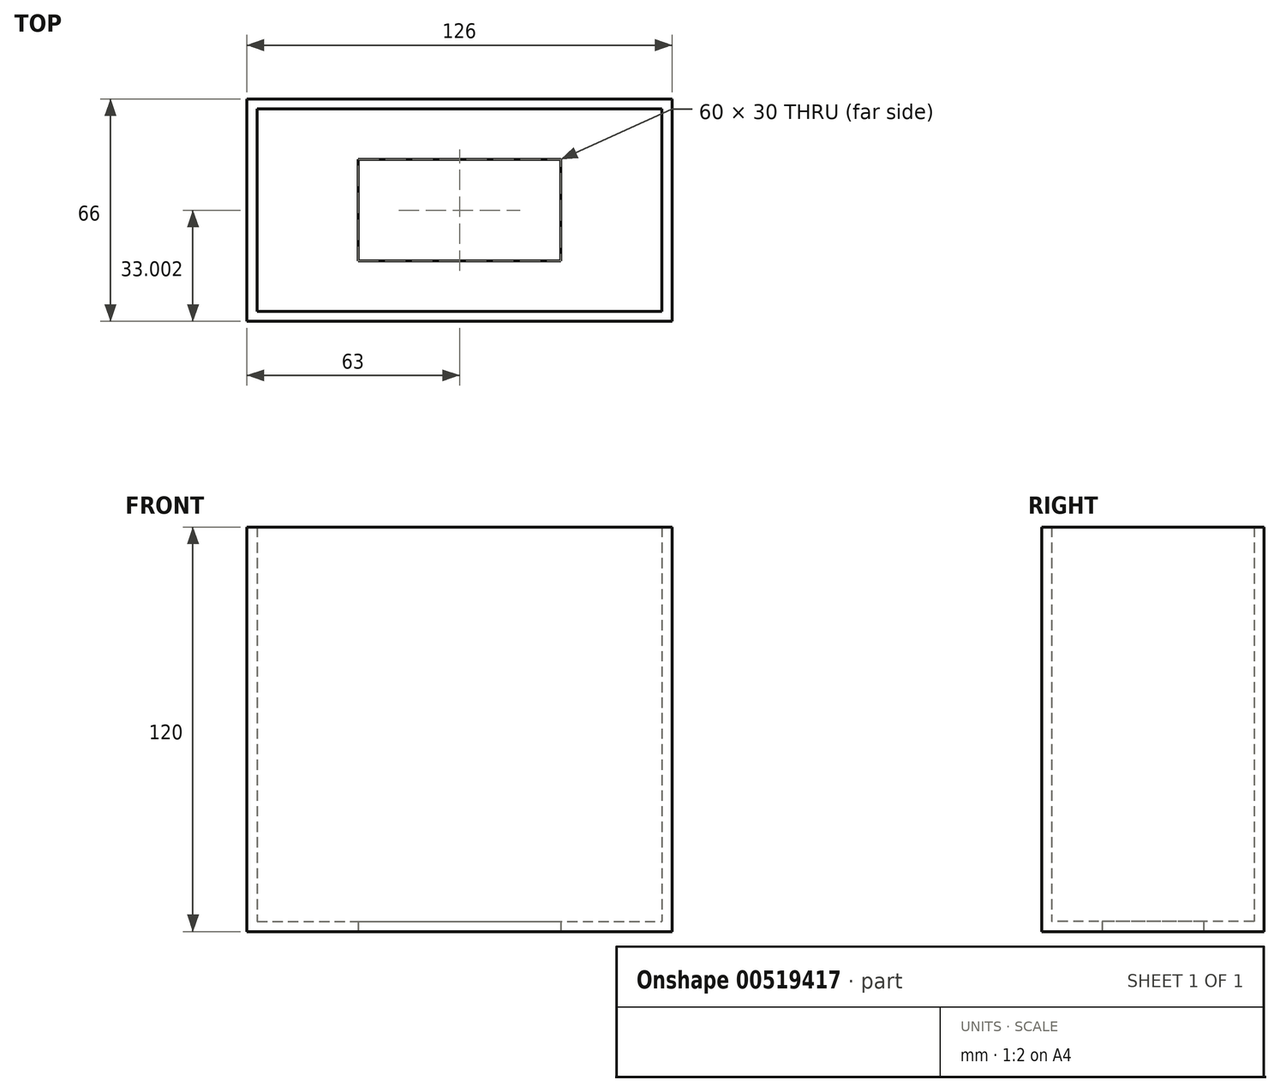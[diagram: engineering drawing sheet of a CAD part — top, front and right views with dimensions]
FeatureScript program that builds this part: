
annotation { "Feature Type Name" : "Feature", "Feature Type Description" : "" }
export const myFeature = defineFeature(function(context is Context, id is Id, definition is map)
    precondition{}
    {
        {
            var Q0;
            Q0=qCreatedBy(makeId("Top.planeOp"),FACE);
            var sketch = newSketch(context, id + "F0", { "sketchPlane" : qUnion([Q0])});
            skLineSegment(sketch, "E0", {"start": v(-93, 53.06) * mm, "end": v(27, 53.06) * mm});
            skLineSegment(sketch, "E1", {"start": v(-93, 53.06) * mm, "end": v(-93, -6.94) * mm});
            skLineSegment(sketch, "E2", {"start": v(-93, -6.94) * mm, "end": v(27, -6.94) * mm});
            skLineSegment(sketch, "E3", {"start": v(27, 53.06) * mm, "end": v(27, -6.94) * mm});
            skLineSegment(sketch, "E4", {"start": v(-96, 56.06) * mm, "end": v(-96, -9.94) * mm});
            skLineSegment(sketch, "E5", {"start": v(-96, 56.06) * mm, "end": v(30, 56.06) * mm});
            skLineSegment(sketch, "E6", {"start": v(-96, -9.94) * mm, "end": v(30, -9.94) * mm});
            skLineSegment(sketch, "E7", {"start": v(30, 56.06) * mm, "end": v(30, -9.94) * mm});
            skLineSegment(sketch, "E8.bottom", {"start": v(-63, 38.06) * mm, "end": v(-3, 38.06) * mm});
            skLineSegment(sketch, "E8.top", {"start": v(-63, 8.06) * mm, "end": v(-3, 8.06) * mm});
            skLineSegment(sketch, "E8.left", {"start": v(-63, 38.06) * mm, "end": v(-63, 8.06) * mm});
            skLineSegment(sketch, "E8.right", {"start": v(-3, 38.06) * mm, "end": v(-3, 8.06) * mm});
            skSolve(sketch);
        }
        {
            var Q0;
            Q0=makeQuery(id+"F0.imprint","IMPRINT",FACE,{"disambiguationData":[TD([[makeQuery(id+"F0.imprint","IMPRINT",EDGE,{"derivedFrom":sQuery(id+"F0.wireOp",EDGE,"E0")}),1.0]])]});
            extrude(context, id + "F1", {"entities" : qUnion([Q0]), "depth" : 120 * mm, "offsetDistance" : 25.4 * mm});
        }
        {
            var Q0;
            Q0=makeQuery(id+"F0.imprint","IMPRINT",FACE,{"disambiguationData":[TD([[makeQuery(id+"F0.imprint","IMPRINT",EDGE,{"derivedFrom":sQuery(id+"F0.wireOp",EDGE,"E0")}),-1.0]])]});
            extrude(context, id + "F2", {"entities" : qUnion([Q0]), "operationType" : NewBodyOperationType.ADD, "depth" : 3 * mm, "offsetDistance" : 25.4 * mm});
        }
    });
